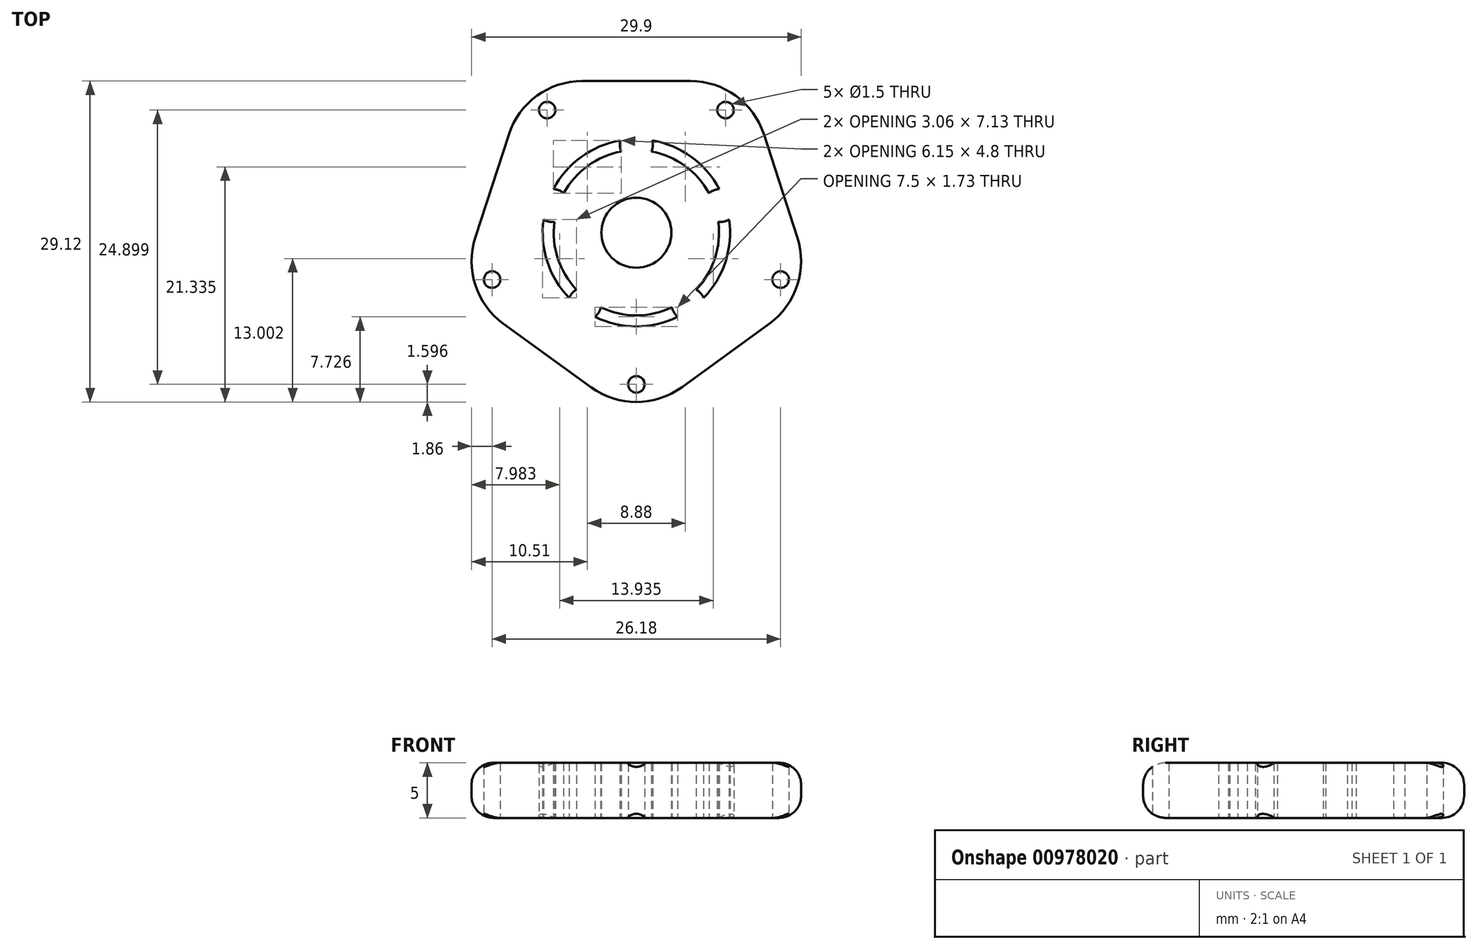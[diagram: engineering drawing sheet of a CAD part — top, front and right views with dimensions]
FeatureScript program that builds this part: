
annotation { "Feature Type Name" : "Feature", "Feature Type Description" : "" }
export const myFeature = defineFeature(function(context is Context, id is Id, definition is map)
    precondition{}
    {
        {
            var Q0;
            Q0=qCreatedBy(makeId("Top.planeOp"),FACE);
            var sketch = newSketch(context, id + "F0", { "sketchPlane" : qUnion([Q0])});
            skCircle(sketch, "E0.cCircle", {"center": v(0, 0) * mm, "radius": 13.76 * mm, "construction": true});
            skLineSegment(sketch, "E0.0", {"start": v(-10, 13.76) * mm, "end": v(10, 13.76) * mm});
            skLineSegment(sketch, "E0.1", {"start": v(10, 13.76) * mm, "end": v(16.18, -5.26) * mm});
            skLineSegment(sketch, "E0.2", {"start": v(16.18, -5.26) * mm, "end": v(0, -17.01) * mm});
            skLineSegment(sketch, "E0.3", {"start": v(0, -17.01) * mm, "end": v(-16.18, -5.26) * mm});
            skLineSegment(sketch, "E0.4", {"start": v(-16.18, -5.26) * mm, "end": v(-10, 13.76) * mm});
            skPoint(sketch, "E0.0.midPoint", {"position": v(0, 13.76) * mm});
            skCircle(sketch, "E1", {"center": v(0, 0) * mm, "radius": 3.18 * mm});
            skLineSegment(sketch, "E2", {"start": v(-10, 13.76) * mm, "end": v(0, 0) * mm, "construction": true});
            skLineSegment(sketch, "E3", {"start": v(10, 13.76) * mm, "end": v(0, 0) * mm, "construction": true});
            skLineSegment(sketch, "E4", {"start": v(16.18, -5.26) * mm, "end": v(0, 0) * mm, "construction": true});
            skLineSegment(sketch, "E5", {"start": v(0, -17.01) * mm, "end": v(0, 0) * mm, "construction": true});
            skLineSegment(sketch, "E6", {"start": v(-16.18, -5.26) * mm, "end": v(0, 0) * mm, "construction": true});
            skCircle(sketch, "E7", {"center": v(-8.1, 11.14) * mm, "radius": 0.75 * mm});
            skCircle(sketch, "E8", {"center": v(8.1, 11.14) * mm, "radius": 0.75 * mm});
            skCircle(sketch, "E9", {"center": v(13.1, -4.25) * mm, "radius": 0.75 * mm});
            skCircle(sketch, "E10", {"center": v(0, -13.76) * mm, "radius": 0.75 * mm});
            skCircle(sketch, "E11", {"center": v(-13.1, -4.25) * mm, "radius": 0.75 * mm});
            skArc(sketch, "E12", {"start": v(-1.36, 7.37) * mm, "mid": v(-4.4, 6.07) * mm, "end": v(-6.6, 3.58) * mm});
            skArc(sketch, "E13", {"start": v(-1.45, 8.38) * mm, "mid": v(-5, 6.88) * mm, "end": v(-7.52, 3.97) * mm});
            skLineSegment(sketch, "E14", {"start": v(0, 8.5) * mm, "end": v(0, 7.5) * mm, "construction": true});
            skLineSegment(sketch, "E15", {"start": v(-8.08, 2.63) * mm, "end": v(-7.13, 2.32) * mm, "construction": true});
            skLineSegment(sketch, "E16", {"start": v(-5, -6.88) * mm, "end": v(-4.4, -6.07) * mm, "construction": true});
            skLineSegment(sketch, "E17", {"start": v(5, -6.88) * mm, "end": v(4.4, -6.07) * mm, "construction": true});
            skLineSegment(sketch, "E18", {"start": v(8.08, 2.63) * mm, "end": v(7.13, 2.32) * mm, "construction": true});
            skPoint(sketch, "E19.orphan", {"position": v(13.1, 4.25) * mm});
            skPoint(sketch, "E20.orphan", {"position": v(-13.1, 4.25) * mm});
            skPoint(sketch, "E21.orphan", {"position": v(-8.1, -11.14) * mm});
            skPoint(sketch, "E22.orphan", {"position": v(8.1, -11.14) * mm});
            skArc(sketch, "E23", {"start": v(-1.45, 8.38) * mm, "mid": v(-1.5, 7.87) * mm, "end": v(-1.36, 7.38) * mm});
            skArc(sketch, "E24.1.0", {"start": v(-8.41, 1.2) * mm, "mid": v(-7.94, 1.01) * mm, "end": v(-7.44, 0.98) * mm});
            skArc(sketch, "E24.2.0", {"start": v(-5.44, -5.17) * mm, "mid": v(-5.83, -5.49) * mm, "end": v(-6.1, -5.92) * mm});
            skArc(sketch, "E24.3.0", {"start": v(3.23, -6.77) * mm, "mid": v(3.42, -7.24) * mm, "end": v(3.75, -7.63) * mm});
            skArc(sketch, "E24.4.0", {"start": v(7.44, 0.98) * mm, "mid": v(7.94, 1.01) * mm, "end": v(8.41, 1.2) * mm});
            skArc(sketch, "E25.trimOffspring", {"start": v(1.36, 7.38) * mm, "mid": v(1.5, 7.87) * mm, "end": v(1.45, 8.38) * mm});
            skArc(sketch, "E26.trimOffspring", {"start": v(7.52, 3.97) * mm, "mid": v(7.02, 3.85) * mm, "end": v(6.6, 3.58) * mm});
            skArc(sketch, "E27.trimOffspring", {"start": v(6.6, 3.58) * mm, "mid": v(4.4, 6.07) * mm, "end": v(1.36, 7.38) * mm});
            skArc(sketch, "E28.trimOffspring", {"start": v(7.52, 3.97) * mm, "mid": v(5, 6.88) * mm, "end": v(1.45, 8.38) * mm});
            skArc(sketch, "E29.trimOffspring", {"start": v(6.1, -5.92) * mm, "mid": v(5.83, -5.49) * mm, "end": v(5.44, -5.17) * mm});
            skArc(sketch, "E30.trimOffspring", {"start": v(6.1, -5.92) * mm, "mid": v(8.08, -2.63) * mm, "end": v(8.41, 1.2) * mm});
            skArc(sketch, "E31.trimOffspring", {"start": v(5.44, -5.17) * mm, "mid": v(7.13, -2.32) * mm, "end": v(7.44, 0.98) * mm});
            skArc(sketch, "E32.trimOffspring", {"start": v(-3.75, -7.63) * mm, "mid": v(-3.42, -7.24) * mm, "end": v(-3.23, -6.77) * mm});
            skArc(sketch, "E33.trimOffspring", {"start": v(-3.23, -6.77) * mm, "mid": v(0, -7.5) * mm, "end": v(3.23, -6.77) * mm});
            skArc(sketch, "E34.trimOffspring", {"start": v(-3.75, -7.63) * mm, "mid": v(0, -8.5) * mm, "end": v(3.75, -7.63) * mm});
            skArc(sketch, "E35.trimOffspring", {"start": v(-6.6, 3.58) * mm, "mid": v(-7.02, 3.85) * mm, "end": v(-7.52, 3.97) * mm});
            skArc(sketch, "E36.trimOffspring", {"start": v(-7.44, 0.98) * mm, "mid": v(-7.13, -2.32) * mm, "end": v(-5.44, -5.17) * mm});
            skArc(sketch, "E37.trimOffspring", {"start": v(-8.41, 1.2) * mm, "mid": v(-8.08, -2.63) * mm, "end": v(-6.1, -5.92) * mm});
            skSolve(sketch);
        }
        {
            var Q0;
            Q0 = qSketchRegion(id + "F0", true);
            extrude(context, id + "F1", {"entities" : qUnion([Q0]), "depth" : 5 * mm, "offsetDistance" : 25 * mm});
        }
        {
            var Q0;
            Q0=makeQuery(id+"F1.opExtrude","SWEPT_EDGE",EDGE,{"disambiguationData":[OSD([sQuery(id+"F0.wireOp",EDGE,"E0.1"),sQuery(id+"F0.wireOp",EDGE,"E0.2")])]});
            var Q1;
            Q1=makeQuery(id+"F1.opExtrude","SWEPT_EDGE",EDGE,{"disambiguationData":[OSD([sQuery(id+"F0.wireOp",EDGE,"E0.0"),sQuery(id+"F0.wireOp",EDGE,"E0.1")])]});
            var Q2;
            Q2=makeQuery(id+"F1.opExtrude","SWEPT_EDGE",EDGE,{"disambiguationData":[OSD([sQuery(id+"F0.wireOp",EDGE,"E0.0"),sQuery(id+"F0.wireOp",EDGE,"E0.4")])]});
            var Q3;
            Q3=makeQuery(id+"F1.opExtrude","SWEPT_EDGE",EDGE,{"disambiguationData":[OSD([sQuery(id+"F0.wireOp",EDGE,"E0.3"),sQuery(id+"F0.wireOp",EDGE,"E0.4")])]});
            var Q4;
            Q4=makeQuery(id+"F1.opExtrude","SWEPT_EDGE",EDGE,{"disambiguationData":[OSD([sQuery(id+"F0.wireOp",EDGE,"E0.2"),sQuery(id+"F0.wireOp",EDGE,"E0.3")])]});
            fillet(context, id + "F2", {"entities" : qUnion([Q0, Q1, Q2, Q3, Q4]), "radius" : 7 * mm, "tangentPropagation" : true, "allowEdgeOverflow" : false});
        }
        {
            var Q0;
            Q0=makeQuery(id+"F1.opExtrude","CAP_EDGE",EDGE,{"disambiguationData":[OSD([sQuery(id+"F0.wireOp",EDGE,"E0.0")])],"isStart":true});
            var Q1;
            {var subQ0=sQuery(id+"F0.wireOp",EDGE,"E0.1");var subQ1=sQuery(id+"F0.wireOp",EDGE,"E0.0");Q1=makeQuery(id+"F2.opFillet","BLEND_EDGE",EDGE,{"blendedFrom":[makeQuery(id+"F1.opExtrude","SWEPT_EDGE",EDGE,{"disambiguationData":[OSD([subQ1,subQ0])]}),makeQuery(id+"F1.opExtrude","CAP_FACE",FACE,{"disambiguationData":[OSD([subQ1,subQ0,sQuery(id+"F0.wireOp",EDGE,"E0.2"),sQuery(id+"F0.wireOp",EDGE,"E0.3"),sQuery(id+"F0.wireOp",EDGE,"E0.4"),sQuery(id+"F0.wireOp",EDGE,"E1"),sQuery(id+"F0.wireOp",EDGE,"E7"),sQuery(id+"F0.wireOp",EDGE,"E8"),sQuery(id+"F0.wireOp",EDGE,"E9"),sQuery(id+"F0.wireOp",EDGE,"E10"),sQuery(id+"F0.wireOp",EDGE,"E11"),sQuery(id+"F0.wireOp",EDGE,"C1mC6EZn-5nCD-hes2-vKRq-OwUpsTl2plRO"),sQuery(id+"F0.wireOp",EDGE,"8d6d3e46-afde-4952-8f6f-9f6e64e2edd4.1.0"),sQuery(id+"F0.wireOp",EDGE,"8d6d3e46-afde-4952-8f6f-9f6e64e2edd4.2.0"),sQuery(id+"F0.wireOp",EDGE,"8d6d3e46-afde-4952-8f6f-9f6e64e2edd4.3.0"),sQuery(id+"F0.wireOp",EDGE,"8d6d3e46-afde-4952-8f6f-9f6e64e2edd4.4.0")])],"isStart":true})],"blendedInto":[makeQuery(id+"F1.opExtrude","CAP_FACE",FACE,{"disambiguationData":[OSD([subQ1,subQ0,sQuery(id+"F0.wireOp",EDGE,"E0.2"),sQuery(id+"F0.wireOp",EDGE,"E0.3"),sQuery(id+"F0.wireOp",EDGE,"E0.4"),sQuery(id+"F0.wireOp",EDGE,"E1"),sQuery(id+"F0.wireOp",EDGE,"E7"),sQuery(id+"F0.wireOp",EDGE,"E8"),sQuery(id+"F0.wireOp",EDGE,"E9"),sQuery(id+"F0.wireOp",EDGE,"E10"),sQuery(id+"F0.wireOp",EDGE,"E11"),sQuery(id+"F0.wireOp",EDGE,"C1mC6EZn-5nCD-hes2-vKRq-OwUpsTl2plRO"),sQuery(id+"F0.wireOp",EDGE,"8d6d3e46-afde-4952-8f6f-9f6e64e2edd4.1.0"),sQuery(id+"F0.wireOp",EDGE,"8d6d3e46-afde-4952-8f6f-9f6e64e2edd4.2.0"),sQuery(id+"F0.wireOp",EDGE,"8d6d3e46-afde-4952-8f6f-9f6e64e2edd4.3.0"),sQuery(id+"F0.wireOp",EDGE,"8d6d3e46-afde-4952-8f6f-9f6e64e2edd4.4.0")])],"isStart":true})]});}
            var Q2;
            Q2=makeQuery(id+"F1.opExtrude","CAP_EDGE",EDGE,{"disambiguationData":[OSD([sQuery(id+"F0.wireOp",EDGE,"E0.1")])],"isStart":true});
            var Q3;
            {var subQ0=sQuery(id+"F0.wireOp",EDGE,"E0.2");var subQ1=sQuery(id+"F0.wireOp",EDGE,"E0.1");Q3=makeQuery(id+"F2.opFillet","BLEND_EDGE",EDGE,{"blendedFrom":[makeQuery(id+"F1.opExtrude","SWEPT_EDGE",EDGE,{"disambiguationData":[OSD([subQ1,subQ0])]}),makeQuery(id+"F1.opExtrude","CAP_FACE",FACE,{"disambiguationData":[OSD([sQuery(id+"F0.wireOp",EDGE,"E0.0"),subQ1,subQ0,sQuery(id+"F0.wireOp",EDGE,"E0.3"),sQuery(id+"F0.wireOp",EDGE,"E0.4"),sQuery(id+"F0.wireOp",EDGE,"E1"),sQuery(id+"F0.wireOp",EDGE,"E7"),sQuery(id+"F0.wireOp",EDGE,"E8"),sQuery(id+"F0.wireOp",EDGE,"E9"),sQuery(id+"F0.wireOp",EDGE,"E10"),sQuery(id+"F0.wireOp",EDGE,"E11"),sQuery(id+"F0.wireOp",EDGE,"C1mC6EZn-5nCD-hes2-vKRq-OwUpsTl2plRO"),sQuery(id+"F0.wireOp",EDGE,"8d6d3e46-afde-4952-8f6f-9f6e64e2edd4.1.0"),sQuery(id+"F0.wireOp",EDGE,"8d6d3e46-afde-4952-8f6f-9f6e64e2edd4.2.0"),sQuery(id+"F0.wireOp",EDGE,"8d6d3e46-afde-4952-8f6f-9f6e64e2edd4.3.0"),sQuery(id+"F0.wireOp",EDGE,"8d6d3e46-afde-4952-8f6f-9f6e64e2edd4.4.0")])],"isStart":true})],"blendedInto":[makeQuery(id+"F1.opExtrude","CAP_FACE",FACE,{"disambiguationData":[OSD([sQuery(id+"F0.wireOp",EDGE,"E0.0"),subQ1,subQ0,sQuery(id+"F0.wireOp",EDGE,"E0.3"),sQuery(id+"F0.wireOp",EDGE,"E0.4"),sQuery(id+"F0.wireOp",EDGE,"E1"),sQuery(id+"F0.wireOp",EDGE,"E7"),sQuery(id+"F0.wireOp",EDGE,"E8"),sQuery(id+"F0.wireOp",EDGE,"E9"),sQuery(id+"F0.wireOp",EDGE,"E10"),sQuery(id+"F0.wireOp",EDGE,"E11"),sQuery(id+"F0.wireOp",EDGE,"C1mC6EZn-5nCD-hes2-vKRq-OwUpsTl2plRO"),sQuery(id+"F0.wireOp",EDGE,"8d6d3e46-afde-4952-8f6f-9f6e64e2edd4.1.0"),sQuery(id+"F0.wireOp",EDGE,"8d6d3e46-afde-4952-8f6f-9f6e64e2edd4.2.0"),sQuery(id+"F0.wireOp",EDGE,"8d6d3e46-afde-4952-8f6f-9f6e64e2edd4.3.0"),sQuery(id+"F0.wireOp",EDGE,"8d6d3e46-afde-4952-8f6f-9f6e64e2edd4.4.0")])],"isStart":true})]});}
            var Q4;
            Q4=makeQuery(id+"F1.opExtrude","CAP_EDGE",EDGE,{"disambiguationData":[OSD([sQuery(id+"F0.wireOp",EDGE,"E0.2")])],"isStart":true});
            var Q5;
            {var subQ0=sQuery(id+"F0.wireOp",EDGE,"E0.3");var subQ1=sQuery(id+"F0.wireOp",EDGE,"E0.2");Q5=makeQuery(id+"F2.opFillet","BLEND_EDGE",EDGE,{"blendedFrom":[makeQuery(id+"F1.opExtrude","SWEPT_EDGE",EDGE,{"disambiguationData":[OSD([subQ1,subQ0])]}),makeQuery(id+"F1.opExtrude","CAP_FACE",FACE,{"disambiguationData":[OSD([sQuery(id+"F0.wireOp",EDGE,"E0.0"),sQuery(id+"F0.wireOp",EDGE,"E0.1"),subQ1,subQ0,sQuery(id+"F0.wireOp",EDGE,"E0.4"),sQuery(id+"F0.wireOp",EDGE,"E1"),sQuery(id+"F0.wireOp",EDGE,"E7"),sQuery(id+"F0.wireOp",EDGE,"E8"),sQuery(id+"F0.wireOp",EDGE,"E9"),sQuery(id+"F0.wireOp",EDGE,"E10"),sQuery(id+"F0.wireOp",EDGE,"E11"),sQuery(id+"F0.wireOp",EDGE,"C1mC6EZn-5nCD-hes2-vKRq-OwUpsTl2plRO"),sQuery(id+"F0.wireOp",EDGE,"8d6d3e46-afde-4952-8f6f-9f6e64e2edd4.1.0"),sQuery(id+"F0.wireOp",EDGE,"8d6d3e46-afde-4952-8f6f-9f6e64e2edd4.2.0"),sQuery(id+"F0.wireOp",EDGE,"8d6d3e46-afde-4952-8f6f-9f6e64e2edd4.3.0"),sQuery(id+"F0.wireOp",EDGE,"8d6d3e46-afde-4952-8f6f-9f6e64e2edd4.4.0")])],"isStart":true})],"blendedInto":[makeQuery(id+"F1.opExtrude","CAP_FACE",FACE,{"disambiguationData":[OSD([sQuery(id+"F0.wireOp",EDGE,"E0.0"),sQuery(id+"F0.wireOp",EDGE,"E0.1"),subQ1,subQ0,sQuery(id+"F0.wireOp",EDGE,"E0.4"),sQuery(id+"F0.wireOp",EDGE,"E1"),sQuery(id+"F0.wireOp",EDGE,"E7"),sQuery(id+"F0.wireOp",EDGE,"E8"),sQuery(id+"F0.wireOp",EDGE,"E9"),sQuery(id+"F0.wireOp",EDGE,"E10"),sQuery(id+"F0.wireOp",EDGE,"E11"),sQuery(id+"F0.wireOp",EDGE,"C1mC6EZn-5nCD-hes2-vKRq-OwUpsTl2plRO"),sQuery(id+"F0.wireOp",EDGE,"8d6d3e46-afde-4952-8f6f-9f6e64e2edd4.1.0"),sQuery(id+"F0.wireOp",EDGE,"8d6d3e46-afde-4952-8f6f-9f6e64e2edd4.2.0"),sQuery(id+"F0.wireOp",EDGE,"8d6d3e46-afde-4952-8f6f-9f6e64e2edd4.3.0"),sQuery(id+"F0.wireOp",EDGE,"8d6d3e46-afde-4952-8f6f-9f6e64e2edd4.4.0")])],"isStart":true})]});}
            var Q6;
            Q6=makeQuery(id+"F1.opExtrude","CAP_EDGE",EDGE,{"disambiguationData":[OSD([sQuery(id+"F0.wireOp",EDGE,"E0.3")])],"isStart":true});
            var Q7;
            {var subQ0=sQuery(id+"F0.wireOp",EDGE,"E0.4");var subQ1=sQuery(id+"F0.wireOp",EDGE,"E0.3");Q7=makeQuery(id+"F2.opFillet","BLEND_EDGE",EDGE,{"blendedFrom":[makeQuery(id+"F1.opExtrude","SWEPT_EDGE",EDGE,{"disambiguationData":[OSD([subQ1,subQ0])]}),makeQuery(id+"F1.opExtrude","CAP_FACE",FACE,{"disambiguationData":[OSD([sQuery(id+"F0.wireOp",EDGE,"E0.0"),sQuery(id+"F0.wireOp",EDGE,"E0.1"),sQuery(id+"F0.wireOp",EDGE,"E0.2"),subQ1,subQ0,sQuery(id+"F0.wireOp",EDGE,"E1"),sQuery(id+"F0.wireOp",EDGE,"E7"),sQuery(id+"F0.wireOp",EDGE,"E8"),sQuery(id+"F0.wireOp",EDGE,"E9"),sQuery(id+"F0.wireOp",EDGE,"E10"),sQuery(id+"F0.wireOp",EDGE,"E11"),sQuery(id+"F0.wireOp",EDGE,"C1mC6EZn-5nCD-hes2-vKRq-OwUpsTl2plRO"),sQuery(id+"F0.wireOp",EDGE,"8d6d3e46-afde-4952-8f6f-9f6e64e2edd4.1.0"),sQuery(id+"F0.wireOp",EDGE,"8d6d3e46-afde-4952-8f6f-9f6e64e2edd4.2.0"),sQuery(id+"F0.wireOp",EDGE,"8d6d3e46-afde-4952-8f6f-9f6e64e2edd4.3.0"),sQuery(id+"F0.wireOp",EDGE,"8d6d3e46-afde-4952-8f6f-9f6e64e2edd4.4.0")])],"isStart":true})],"blendedInto":[makeQuery(id+"F1.opExtrude","CAP_FACE",FACE,{"disambiguationData":[OSD([sQuery(id+"F0.wireOp",EDGE,"E0.0"),sQuery(id+"F0.wireOp",EDGE,"E0.1"),sQuery(id+"F0.wireOp",EDGE,"E0.2"),subQ1,subQ0,sQuery(id+"F0.wireOp",EDGE,"E1"),sQuery(id+"F0.wireOp",EDGE,"E7"),sQuery(id+"F0.wireOp",EDGE,"E8"),sQuery(id+"F0.wireOp",EDGE,"E9"),sQuery(id+"F0.wireOp",EDGE,"E10"),sQuery(id+"F0.wireOp",EDGE,"E11"),sQuery(id+"F0.wireOp",EDGE,"C1mC6EZn-5nCD-hes2-vKRq-OwUpsTl2plRO"),sQuery(id+"F0.wireOp",EDGE,"8d6d3e46-afde-4952-8f6f-9f6e64e2edd4.1.0"),sQuery(id+"F0.wireOp",EDGE,"8d6d3e46-afde-4952-8f6f-9f6e64e2edd4.2.0"),sQuery(id+"F0.wireOp",EDGE,"8d6d3e46-afde-4952-8f6f-9f6e64e2edd4.3.0"),sQuery(id+"F0.wireOp",EDGE,"8d6d3e46-afde-4952-8f6f-9f6e64e2edd4.4.0")])],"isStart":true})]});}
            var Q8;
            Q8=makeQuery(id+"F1.opExtrude","CAP_EDGE",EDGE,{"disambiguationData":[OSD([sQuery(id+"F0.wireOp",EDGE,"E0.4")])],"isStart":true});
            var Q9;
            {var subQ0=sQuery(id+"F0.wireOp",EDGE,"E0.4");var subQ1=sQuery(id+"F0.wireOp",EDGE,"E0.0");Q9=makeQuery(id+"F2.opFillet","BLEND_EDGE",EDGE,{"blendedFrom":[makeQuery(id+"F1.opExtrude","SWEPT_EDGE",EDGE,{"disambiguationData":[OSD([subQ1,subQ0])]}),makeQuery(id+"F1.opExtrude","CAP_FACE",FACE,{"disambiguationData":[OSD([subQ1,sQuery(id+"F0.wireOp",EDGE,"E0.1"),sQuery(id+"F0.wireOp",EDGE,"E0.2"),sQuery(id+"F0.wireOp",EDGE,"E0.3"),subQ0,sQuery(id+"F0.wireOp",EDGE,"E1"),sQuery(id+"F0.wireOp",EDGE,"E7"),sQuery(id+"F0.wireOp",EDGE,"E8"),sQuery(id+"F0.wireOp",EDGE,"E9"),sQuery(id+"F0.wireOp",EDGE,"E10"),sQuery(id+"F0.wireOp",EDGE,"E11"),sQuery(id+"F0.wireOp",EDGE,"C1mC6EZn-5nCD-hes2-vKRq-OwUpsTl2plRO"),sQuery(id+"F0.wireOp",EDGE,"8d6d3e46-afde-4952-8f6f-9f6e64e2edd4.1.0"),sQuery(id+"F0.wireOp",EDGE,"8d6d3e46-afde-4952-8f6f-9f6e64e2edd4.2.0"),sQuery(id+"F0.wireOp",EDGE,"8d6d3e46-afde-4952-8f6f-9f6e64e2edd4.3.0"),sQuery(id+"F0.wireOp",EDGE,"8d6d3e46-afde-4952-8f6f-9f6e64e2edd4.4.0")])],"isStart":true})],"blendedInto":[makeQuery(id+"F1.opExtrude","CAP_FACE",FACE,{"disambiguationData":[OSD([subQ1,sQuery(id+"F0.wireOp",EDGE,"E0.1"),sQuery(id+"F0.wireOp",EDGE,"E0.2"),sQuery(id+"F0.wireOp",EDGE,"E0.3"),subQ0,sQuery(id+"F0.wireOp",EDGE,"E1"),sQuery(id+"F0.wireOp",EDGE,"E7"),sQuery(id+"F0.wireOp",EDGE,"E8"),sQuery(id+"F0.wireOp",EDGE,"E9"),sQuery(id+"F0.wireOp",EDGE,"E10"),sQuery(id+"F0.wireOp",EDGE,"E11"),sQuery(id+"F0.wireOp",EDGE,"C1mC6EZn-5nCD-hes2-vKRq-OwUpsTl2plRO"),sQuery(id+"F0.wireOp",EDGE,"8d6d3e46-afde-4952-8f6f-9f6e64e2edd4.1.0"),sQuery(id+"F0.wireOp",EDGE,"8d6d3e46-afde-4952-8f6f-9f6e64e2edd4.2.0"),sQuery(id+"F0.wireOp",EDGE,"8d6d3e46-afde-4952-8f6f-9f6e64e2edd4.3.0"),sQuery(id+"F0.wireOp",EDGE,"8d6d3e46-afde-4952-8f6f-9f6e64e2edd4.4.0")])],"isStart":true})]});}
            fillet(context, id + "F3", {"entities" : qUnion([Q0, Q1, Q2, Q3, Q4, Q5, Q6, Q7, Q8, Q9]), "radius" : 2 * mm, "tangentPropagation" : true, "allowEdgeOverflow" : false});
        }
        {
            var Q0;
            Q0=makeQuery(id+"F1.opExtrude","CAP_EDGE",EDGE,{"disambiguationData":[OSD([sQuery(id+"F0.wireOp",EDGE,"E0.0")])],"isStart":false});
            var Q1;
            {var subQ0=sQuery(id+"F0.wireOp",EDGE,"E0.1");var subQ1=sQuery(id+"F0.wireOp",EDGE,"E0.0");Q1=makeQuery(id+"F2.opFillet","BLEND_EDGE",EDGE,{"blendedFrom":[makeQuery(id+"F1.opExtrude","SWEPT_EDGE",EDGE,{"disambiguationData":[OSD([subQ1,subQ0])]}),makeQuery(id+"F1.opExtrude","CAP_FACE",FACE,{"disambiguationData":[OSD([subQ1,subQ0,sQuery(id+"F0.wireOp",EDGE,"E0.2"),sQuery(id+"F0.wireOp",EDGE,"E0.3"),sQuery(id+"F0.wireOp",EDGE,"E0.4"),sQuery(id+"F0.wireOp",EDGE,"E1"),sQuery(id+"F0.wireOp",EDGE,"E7"),sQuery(id+"F0.wireOp",EDGE,"E8"),sQuery(id+"F0.wireOp",EDGE,"E9"),sQuery(id+"F0.wireOp",EDGE,"E10"),sQuery(id+"F0.wireOp",EDGE,"E11"),sQuery(id+"F0.wireOp",EDGE,"C1mC6EZn-5nCD-hes2-vKRq-OwUpsTl2plRO"),sQuery(id+"F0.wireOp",EDGE,"8d6d3e46-afde-4952-8f6f-9f6e64e2edd4.1.0"),sQuery(id+"F0.wireOp",EDGE,"8d6d3e46-afde-4952-8f6f-9f6e64e2edd4.2.0"),sQuery(id+"F0.wireOp",EDGE,"8d6d3e46-afde-4952-8f6f-9f6e64e2edd4.3.0"),sQuery(id+"F0.wireOp",EDGE,"8d6d3e46-afde-4952-8f6f-9f6e64e2edd4.4.0")])],"isStart":false})],"blendedInto":[makeQuery(id+"F1.opExtrude","CAP_FACE",FACE,{"disambiguationData":[OSD([subQ1,subQ0,sQuery(id+"F0.wireOp",EDGE,"E0.2"),sQuery(id+"F0.wireOp",EDGE,"E0.3"),sQuery(id+"F0.wireOp",EDGE,"E0.4"),sQuery(id+"F0.wireOp",EDGE,"E1"),sQuery(id+"F0.wireOp",EDGE,"E7"),sQuery(id+"F0.wireOp",EDGE,"E8"),sQuery(id+"F0.wireOp",EDGE,"E9"),sQuery(id+"F0.wireOp",EDGE,"E10"),sQuery(id+"F0.wireOp",EDGE,"E11"),sQuery(id+"F0.wireOp",EDGE,"C1mC6EZn-5nCD-hes2-vKRq-OwUpsTl2plRO"),sQuery(id+"F0.wireOp",EDGE,"8d6d3e46-afde-4952-8f6f-9f6e64e2edd4.1.0"),sQuery(id+"F0.wireOp",EDGE,"8d6d3e46-afde-4952-8f6f-9f6e64e2edd4.2.0"),sQuery(id+"F0.wireOp",EDGE,"8d6d3e46-afde-4952-8f6f-9f6e64e2edd4.3.0"),sQuery(id+"F0.wireOp",EDGE,"8d6d3e46-afde-4952-8f6f-9f6e64e2edd4.4.0")])],"isStart":false})]});}
            var Q2;
            {var subQ0=sQuery(id+"F0.wireOp",EDGE,"E0.4");var subQ1=sQuery(id+"F0.wireOp",EDGE,"E0.0");Q2=makeQuery(id+"F2.opFillet","BLEND_EDGE",EDGE,{"blendedFrom":[makeQuery(id+"F1.opExtrude","SWEPT_EDGE",EDGE,{"disambiguationData":[OSD([subQ1,subQ0])]}),makeQuery(id+"F1.opExtrude","CAP_FACE",FACE,{"disambiguationData":[OSD([subQ1,sQuery(id+"F0.wireOp",EDGE,"E0.1"),sQuery(id+"F0.wireOp",EDGE,"E0.2"),sQuery(id+"F0.wireOp",EDGE,"E0.3"),subQ0,sQuery(id+"F0.wireOp",EDGE,"E1"),sQuery(id+"F0.wireOp",EDGE,"E7"),sQuery(id+"F0.wireOp",EDGE,"E8"),sQuery(id+"F0.wireOp",EDGE,"E9"),sQuery(id+"F0.wireOp",EDGE,"E10"),sQuery(id+"F0.wireOp",EDGE,"E11"),sQuery(id+"F0.wireOp",EDGE,"C1mC6EZn-5nCD-hes2-vKRq-OwUpsTl2plRO"),sQuery(id+"F0.wireOp",EDGE,"8d6d3e46-afde-4952-8f6f-9f6e64e2edd4.1.0"),sQuery(id+"F0.wireOp",EDGE,"8d6d3e46-afde-4952-8f6f-9f6e64e2edd4.2.0"),sQuery(id+"F0.wireOp",EDGE,"8d6d3e46-afde-4952-8f6f-9f6e64e2edd4.3.0"),sQuery(id+"F0.wireOp",EDGE,"8d6d3e46-afde-4952-8f6f-9f6e64e2edd4.4.0")])],"isStart":false})],"blendedInto":[makeQuery(id+"F1.opExtrude","CAP_FACE",FACE,{"disambiguationData":[OSD([subQ1,sQuery(id+"F0.wireOp",EDGE,"E0.1"),sQuery(id+"F0.wireOp",EDGE,"E0.2"),sQuery(id+"F0.wireOp",EDGE,"E0.3"),subQ0,sQuery(id+"F0.wireOp",EDGE,"E1"),sQuery(id+"F0.wireOp",EDGE,"E7"),sQuery(id+"F0.wireOp",EDGE,"E8"),sQuery(id+"F0.wireOp",EDGE,"E9"),sQuery(id+"F0.wireOp",EDGE,"E10"),sQuery(id+"F0.wireOp",EDGE,"E11"),sQuery(id+"F0.wireOp",EDGE,"C1mC6EZn-5nCD-hes2-vKRq-OwUpsTl2plRO"),sQuery(id+"F0.wireOp",EDGE,"8d6d3e46-afde-4952-8f6f-9f6e64e2edd4.1.0"),sQuery(id+"F0.wireOp",EDGE,"8d6d3e46-afde-4952-8f6f-9f6e64e2edd4.2.0"),sQuery(id+"F0.wireOp",EDGE,"8d6d3e46-afde-4952-8f6f-9f6e64e2edd4.3.0"),sQuery(id+"F0.wireOp",EDGE,"8d6d3e46-afde-4952-8f6f-9f6e64e2edd4.4.0")])],"isStart":false})]});}
            var Q3;
            Q3=makeQuery(id+"F1.opExtrude","CAP_EDGE",EDGE,{"disambiguationData":[OSD([sQuery(id+"F0.wireOp",EDGE,"E0.1")])],"isStart":false});
            var Q4;
            {var subQ0=sQuery(id+"F0.wireOp",EDGE,"E0.2");var subQ1=sQuery(id+"F0.wireOp",EDGE,"E0.1");Q4=makeQuery(id+"F2.opFillet","BLEND_EDGE",EDGE,{"blendedFrom":[makeQuery(id+"F1.opExtrude","SWEPT_EDGE",EDGE,{"disambiguationData":[OSD([subQ1,subQ0])]}),makeQuery(id+"F1.opExtrude","CAP_FACE",FACE,{"disambiguationData":[OSD([sQuery(id+"F0.wireOp",EDGE,"E0.0"),subQ1,subQ0,sQuery(id+"F0.wireOp",EDGE,"E0.3"),sQuery(id+"F0.wireOp",EDGE,"E0.4"),sQuery(id+"F0.wireOp",EDGE,"E1"),sQuery(id+"F0.wireOp",EDGE,"E7"),sQuery(id+"F0.wireOp",EDGE,"E8"),sQuery(id+"F0.wireOp",EDGE,"E9"),sQuery(id+"F0.wireOp",EDGE,"E10"),sQuery(id+"F0.wireOp",EDGE,"E11"),sQuery(id+"F0.wireOp",EDGE,"C1mC6EZn-5nCD-hes2-vKRq-OwUpsTl2plRO"),sQuery(id+"F0.wireOp",EDGE,"8d6d3e46-afde-4952-8f6f-9f6e64e2edd4.1.0"),sQuery(id+"F0.wireOp",EDGE,"8d6d3e46-afde-4952-8f6f-9f6e64e2edd4.2.0"),sQuery(id+"F0.wireOp",EDGE,"8d6d3e46-afde-4952-8f6f-9f6e64e2edd4.3.0"),sQuery(id+"F0.wireOp",EDGE,"8d6d3e46-afde-4952-8f6f-9f6e64e2edd4.4.0")])],"isStart":false})],"blendedInto":[makeQuery(id+"F1.opExtrude","CAP_FACE",FACE,{"disambiguationData":[OSD([sQuery(id+"F0.wireOp",EDGE,"E0.0"),subQ1,subQ0,sQuery(id+"F0.wireOp",EDGE,"E0.3"),sQuery(id+"F0.wireOp",EDGE,"E0.4"),sQuery(id+"F0.wireOp",EDGE,"E1"),sQuery(id+"F0.wireOp",EDGE,"E7"),sQuery(id+"F0.wireOp",EDGE,"E8"),sQuery(id+"F0.wireOp",EDGE,"E9"),sQuery(id+"F0.wireOp",EDGE,"E10"),sQuery(id+"F0.wireOp",EDGE,"E11"),sQuery(id+"F0.wireOp",EDGE,"C1mC6EZn-5nCD-hes2-vKRq-OwUpsTl2plRO"),sQuery(id+"F0.wireOp",EDGE,"8d6d3e46-afde-4952-8f6f-9f6e64e2edd4.1.0"),sQuery(id+"F0.wireOp",EDGE,"8d6d3e46-afde-4952-8f6f-9f6e64e2edd4.2.0"),sQuery(id+"F0.wireOp",EDGE,"8d6d3e46-afde-4952-8f6f-9f6e64e2edd4.3.0"),sQuery(id+"F0.wireOp",EDGE,"8d6d3e46-afde-4952-8f6f-9f6e64e2edd4.4.0")])],"isStart":false})]});}
            var Q5;
            Q5=makeQuery(id+"F1.opExtrude","CAP_EDGE",EDGE,{"disambiguationData":[OSD([sQuery(id+"F0.wireOp",EDGE,"E0.2")])],"isStart":false});
            var Q6;
            {var subQ0=sQuery(id+"F0.wireOp",EDGE,"E0.3");var subQ1=sQuery(id+"F0.wireOp",EDGE,"E0.2");Q6=makeQuery(id+"F2.opFillet","BLEND_EDGE",EDGE,{"blendedFrom":[makeQuery(id+"F1.opExtrude","SWEPT_EDGE",EDGE,{"disambiguationData":[OSD([subQ1,subQ0])]}),makeQuery(id+"F1.opExtrude","CAP_FACE",FACE,{"disambiguationData":[OSD([sQuery(id+"F0.wireOp",EDGE,"E0.0"),sQuery(id+"F0.wireOp",EDGE,"E0.1"),subQ1,subQ0,sQuery(id+"F0.wireOp",EDGE,"E0.4"),sQuery(id+"F0.wireOp",EDGE,"E1"),sQuery(id+"F0.wireOp",EDGE,"E7"),sQuery(id+"F0.wireOp",EDGE,"E8"),sQuery(id+"F0.wireOp",EDGE,"E9"),sQuery(id+"F0.wireOp",EDGE,"E10"),sQuery(id+"F0.wireOp",EDGE,"E11"),sQuery(id+"F0.wireOp",EDGE,"C1mC6EZn-5nCD-hes2-vKRq-OwUpsTl2plRO"),sQuery(id+"F0.wireOp",EDGE,"8d6d3e46-afde-4952-8f6f-9f6e64e2edd4.1.0"),sQuery(id+"F0.wireOp",EDGE,"8d6d3e46-afde-4952-8f6f-9f6e64e2edd4.2.0"),sQuery(id+"F0.wireOp",EDGE,"8d6d3e46-afde-4952-8f6f-9f6e64e2edd4.3.0"),sQuery(id+"F0.wireOp",EDGE,"8d6d3e46-afde-4952-8f6f-9f6e64e2edd4.4.0")])],"isStart":false})],"blendedInto":[makeQuery(id+"F1.opExtrude","CAP_FACE",FACE,{"disambiguationData":[OSD([sQuery(id+"F0.wireOp",EDGE,"E0.0"),sQuery(id+"F0.wireOp",EDGE,"E0.1"),subQ1,subQ0,sQuery(id+"F0.wireOp",EDGE,"E0.4"),sQuery(id+"F0.wireOp",EDGE,"E1"),sQuery(id+"F0.wireOp",EDGE,"E7"),sQuery(id+"F0.wireOp",EDGE,"E8"),sQuery(id+"F0.wireOp",EDGE,"E9"),sQuery(id+"F0.wireOp",EDGE,"E10"),sQuery(id+"F0.wireOp",EDGE,"E11"),sQuery(id+"F0.wireOp",EDGE,"C1mC6EZn-5nCD-hes2-vKRq-OwUpsTl2plRO"),sQuery(id+"F0.wireOp",EDGE,"8d6d3e46-afde-4952-8f6f-9f6e64e2edd4.1.0"),sQuery(id+"F0.wireOp",EDGE,"8d6d3e46-afde-4952-8f6f-9f6e64e2edd4.2.0"),sQuery(id+"F0.wireOp",EDGE,"8d6d3e46-afde-4952-8f6f-9f6e64e2edd4.3.0"),sQuery(id+"F0.wireOp",EDGE,"8d6d3e46-afde-4952-8f6f-9f6e64e2edd4.4.0")])],"isStart":false})]});}
            var Q7;
            Q7=makeQuery(id+"F1.opExtrude","CAP_EDGE",EDGE,{"disambiguationData":[OSD([sQuery(id+"F0.wireOp",EDGE,"E0.4")])],"isStart":false});
            var Q8;
            {var subQ0=sQuery(id+"F0.wireOp",EDGE,"E0.4");var subQ1=sQuery(id+"F0.wireOp",EDGE,"E0.3");Q8=makeQuery(id+"F2.opFillet","BLEND_EDGE",EDGE,{"blendedFrom":[makeQuery(id+"F1.opExtrude","SWEPT_EDGE",EDGE,{"disambiguationData":[OSD([subQ1,subQ0])]}),makeQuery(id+"F1.opExtrude","CAP_FACE",FACE,{"disambiguationData":[OSD([sQuery(id+"F0.wireOp",EDGE,"E0.0"),sQuery(id+"F0.wireOp",EDGE,"E0.1"),sQuery(id+"F0.wireOp",EDGE,"E0.2"),subQ1,subQ0,sQuery(id+"F0.wireOp",EDGE,"E1"),sQuery(id+"F0.wireOp",EDGE,"E7"),sQuery(id+"F0.wireOp",EDGE,"E8"),sQuery(id+"F0.wireOp",EDGE,"E9"),sQuery(id+"F0.wireOp",EDGE,"E10"),sQuery(id+"F0.wireOp",EDGE,"E11"),sQuery(id+"F0.wireOp",EDGE,"C1mC6EZn-5nCD-hes2-vKRq-OwUpsTl2plRO"),sQuery(id+"F0.wireOp",EDGE,"8d6d3e46-afde-4952-8f6f-9f6e64e2edd4.1.0"),sQuery(id+"F0.wireOp",EDGE,"8d6d3e46-afde-4952-8f6f-9f6e64e2edd4.2.0"),sQuery(id+"F0.wireOp",EDGE,"8d6d3e46-afde-4952-8f6f-9f6e64e2edd4.3.0"),sQuery(id+"F0.wireOp",EDGE,"8d6d3e46-afde-4952-8f6f-9f6e64e2edd4.4.0")])],"isStart":false})],"blendedInto":[makeQuery(id+"F1.opExtrude","CAP_FACE",FACE,{"disambiguationData":[OSD([sQuery(id+"F0.wireOp",EDGE,"E0.0"),sQuery(id+"F0.wireOp",EDGE,"E0.1"),sQuery(id+"F0.wireOp",EDGE,"E0.2"),subQ1,subQ0,sQuery(id+"F0.wireOp",EDGE,"E1"),sQuery(id+"F0.wireOp",EDGE,"E7"),sQuery(id+"F0.wireOp",EDGE,"E8"),sQuery(id+"F0.wireOp",EDGE,"E9"),sQuery(id+"F0.wireOp",EDGE,"E10"),sQuery(id+"F0.wireOp",EDGE,"E11"),sQuery(id+"F0.wireOp",EDGE,"C1mC6EZn-5nCD-hes2-vKRq-OwUpsTl2plRO"),sQuery(id+"F0.wireOp",EDGE,"8d6d3e46-afde-4952-8f6f-9f6e64e2edd4.1.0"),sQuery(id+"F0.wireOp",EDGE,"8d6d3e46-afde-4952-8f6f-9f6e64e2edd4.2.0"),sQuery(id+"F0.wireOp",EDGE,"8d6d3e46-afde-4952-8f6f-9f6e64e2edd4.3.0"),sQuery(id+"F0.wireOp",EDGE,"8d6d3e46-afde-4952-8f6f-9f6e64e2edd4.4.0")])],"isStart":false})]});}
            var Q9;
            Q9=makeQuery(id+"F1.opExtrude","CAP_EDGE",EDGE,{"disambiguationData":[OSD([sQuery(id+"F0.wireOp",EDGE,"E0.3")])],"isStart":false});
            fillet(context, id + "F4", {"entities" : qUnion([Q0, Q1, Q2, Q3, Q4, Q5, Q6, Q7, Q8, Q9]), "radius" : 2 * mm, "tangentPropagation" : true, "allowEdgeOverflow" : false});
        }
    });
